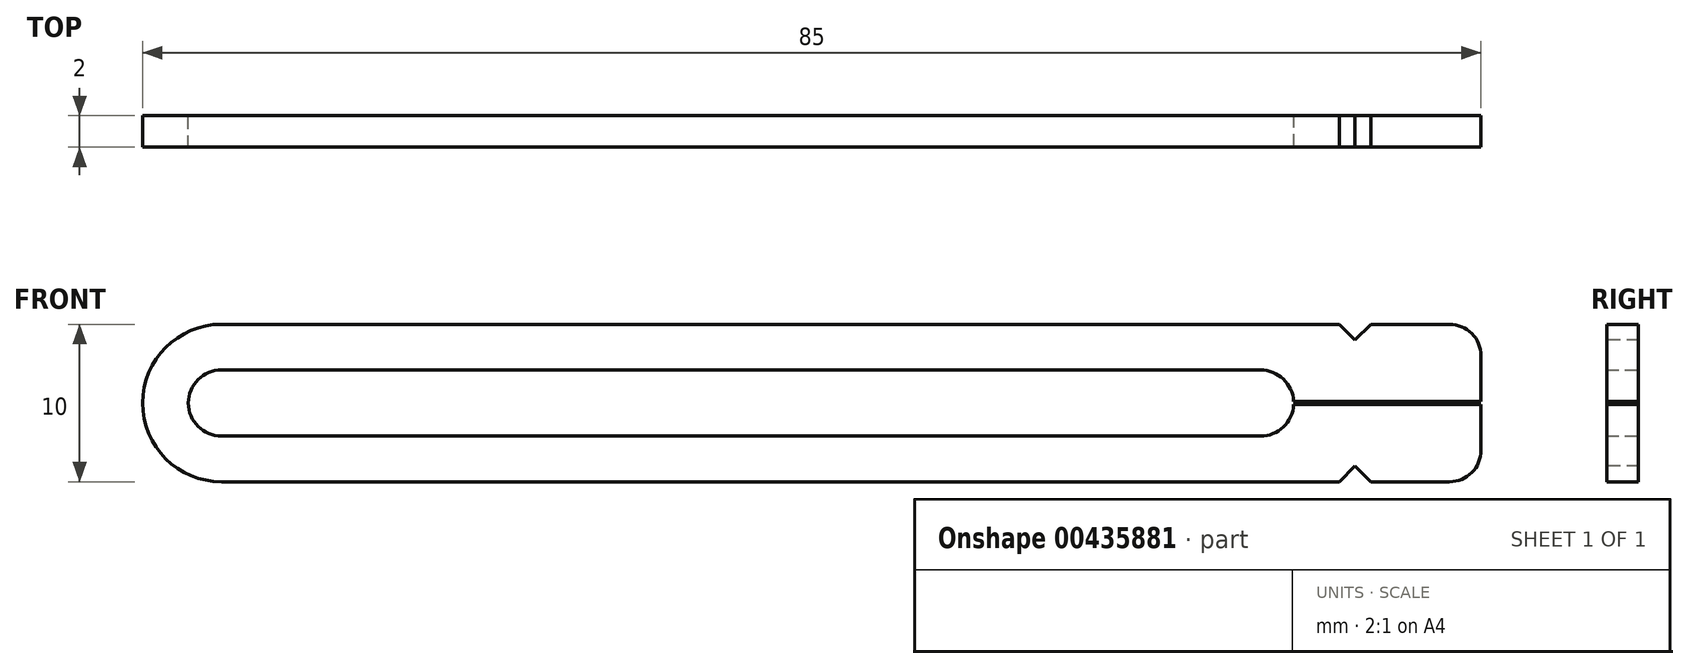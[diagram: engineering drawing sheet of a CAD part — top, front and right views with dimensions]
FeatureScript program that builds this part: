
annotation { "Feature Type Name" : "Feature", "Feature Type Description" : "" }
export const myFeature = defineFeature(function(context is Context, id is Id, definition is map)
    precondition{}
    {
        {
            var Q0;
            Q0=qCreatedBy(makeId("Front.planeOp"),FACE);
            var sketch = newSketch(context, id + "F0", { "sketchPlane" : qUnion([Q0])});
            skLineSegment(sketch, "E0.bottom", {"start": v(0, 5) * mm, "end": v(80, 5) * mm});
            skLineSegment(sketch, "E0.top", {"start": v(0, -5) * mm, "end": v(80, -5) * mm});
            skLineSegment(sketch, "E0.right", {"start": v(80, 5) * mm, "end": v(80, -5) * mm});
            skPoint(sketch, "E1", {"position": v(0, 0) * mm});
            skLineSegment(sketch, "E2", {"start": v(0, 0) * mm, "end": v(66, 0) * mm, "construction": true});
            skArc(sketch, "E3.0.startCap", {"start": v(0, -2.1) * mm, "mid": v(-2.1, 0) * mm, "end": v(0, 2.1) * mm});
            skArc(sketch, "E3.0.endCap", {"start": v(66, 2.1) * mm, "mid": v(68.1, 0) * mm, "end": v(66, -2.1) * mm});
            skLineSegment(sketch, "E3.0.left", {"start": v(0, 2.1) * mm, "end": v(66, 2.1) * mm});
            skLineSegment(sketch, "E3.0.right", {"start": v(0, -2.1) * mm, "end": v(66, -2.1) * mm});
            skArc(sketch, "E4", {"start": v(0, 5) * mm, "mid": v(-5, 0) * mm, "end": v(0, -5) * mm});
            skSolve(sketch);
        }
        {
            var Q0;
            Q0 = qSketchRegion(id + "F0", true);
            extrude(context, id + "F1", {"entities" : qUnion([Q0]), "depth" : 2 * mm});
        }
        {
            var Q0;
            Q0=makeQuery(id+"F1.opExtrude","CAP_FACE",FACE,{"disambiguationData":[OSD([sQuery(id+"F0.wireOp",EDGE,"E0.bottom"),sQuery(id+"F0.wireOp",EDGE,"E0.top"),sQuery(id+"F0.wireOp",EDGE,"E0.right"),sQuery(id+"F0.wireOp",EDGE,"E3.0.startCap"),sQuery(id+"F0.wireOp",EDGE,"E3.0.endCap"),sQuery(id+"F0.wireOp",EDGE,"E3.0.left"),sQuery(id+"F0.wireOp",EDGE,"E3.0.right"),sQuery(id+"F0.wireOp",EDGE,"E4")])],"isStart":false});
            var sketch = newSketch(context, id + "F2", { "sketchPlane" : qUnion([Q0])});
            skLineSegment(sketch, "E5", {"start": v(71, 5) * mm, "end": v(72, 4) * mm});
            skLineSegment(sketch, "E6", {"start": v(72, 4) * mm, "end": v(73, 5) * mm});
            skLineSegment(sketch, "E7", {"start": v(80, 0) * mm, "end": v(0, 0) * mm, "construction": true});
            skLineSegment(sketch, "E8", {"start": v(72, 5) * mm, "end": v(72, -5) * mm, "construction": true});
            skLineSegment(sketch, "E9", {"start": v(73, 5) * mm, "end": v(71, 5) * mm});
            skLineSegment(sketch, "E10.MirrorCS", {"start": v(72, -4) * mm, "end": v(73, -5) * mm});
            skLineSegment(sketch, "E11.MirrorCS", {"start": v(71, -5) * mm, "end": v(72, -4) * mm});
            skLineSegment(sketch, "E12.MirrorCS", {"start": v(73, -5) * mm, "end": v(71, -5) * mm});
            skSolve(sketch);
        }
        {
            var Q0;
            Q0 = qSketchRegion(id + "F2", true);
            extrude(context, id + "F3", {"entities" : qUnion([Q0]), "operationType" : NewBodyOperationType.REMOVE, "endBound" : BoundingType.THROUGH_ALL, "oppositeDirection" : true, "depth" : 25 * mm});
        }
        {
            var Q0;
            Q0=makeQuery(id+"F1.opExtrude","SWEPT_EDGE",EDGE,{"disambiguationData":[OSD([sQuery(id+"F0.wireOp",EDGE,"E0.bottom"),sQuery(id+"F0.wireOp",EDGE,"E0.right")])]});
            var Q1;
            Q1=makeQuery(id+"F1.opExtrude","SWEPT_EDGE",EDGE,{"disambiguationData":[OSD([sQuery(id+"F0.wireOp",EDGE,"E0.top"),sQuery(id+"F0.wireOp",EDGE,"E0.right")])]});
            fillet(context, id + "F4", {"entities" : qUnion([Q0, Q1]), "radius" : 2 * mm, "tangentPropagation" : true, "allowEdgeOverflow" : false});
        }
        {
            var Q0;
            Q0=makeQuery(id+"F1.opExtrude","CAP_FACE",FACE,{"disambiguationData":[OSD([sQuery(id+"F0.wireOp",EDGE,"E0.bottom"),sQuery(id+"F0.wireOp",EDGE,"E0.top"),sQuery(id+"F0.wireOp",EDGE,"E0.right"),sQuery(id+"F0.wireOp",EDGE,"E3.0.startCap"),sQuery(id+"F0.wireOp",EDGE,"E3.0.endCap"),sQuery(id+"F0.wireOp",EDGE,"E3.0.left"),sQuery(id+"F0.wireOp",EDGE,"E3.0.right"),sQuery(id+"F0.wireOp",EDGE,"E4")])],"isStart":false});
            var sketch = newSketch(context, id + "F5", { "sketchPlane" : qUnion([Q0])});
            skLineSegment(sketch, "E13", {"start": v(80, 0.1) * mm, "end": v(68.1, 0.1) * mm});
            skLineSegment(sketch, "E14", {"start": v(80, -0.1) * mm, "end": v(68.1, -0.1) * mm});
            skLineSegment(sketch, "E15", {"start": v(80, 0) * mm, "end": v(68.1, 0) * mm, "construction": true});
            skArc(sketch, "E16.0", {"start": v(68.1, 0.1) * mm, "mid": v(68.1, 0) * mm, "end": v(68.1, -0.1) * mm});
            skLineSegment(sketch, "E17", {"start": v(80, 0.1) * mm, "end": v(80, -0.1) * mm});
            skPoint(sketch, "E18.orphan", {"position": v(66, 2.1) * mm});
            skPoint(sketch, "E19.orphan", {"position": v(66, -2.1) * mm});
            skSolve(sketch);
        }
        {
            var Q0;
            Q0 = qSketchRegion(id + "F5", true);
            extrude(context, id + "F6", {"entities" : qUnion([Q0]), "operationType" : NewBodyOperationType.REMOVE, "endBound" : BoundingType.THROUGH_ALL, "oppositeDirection" : true, "depth" : 25 * mm});
        }
    });
